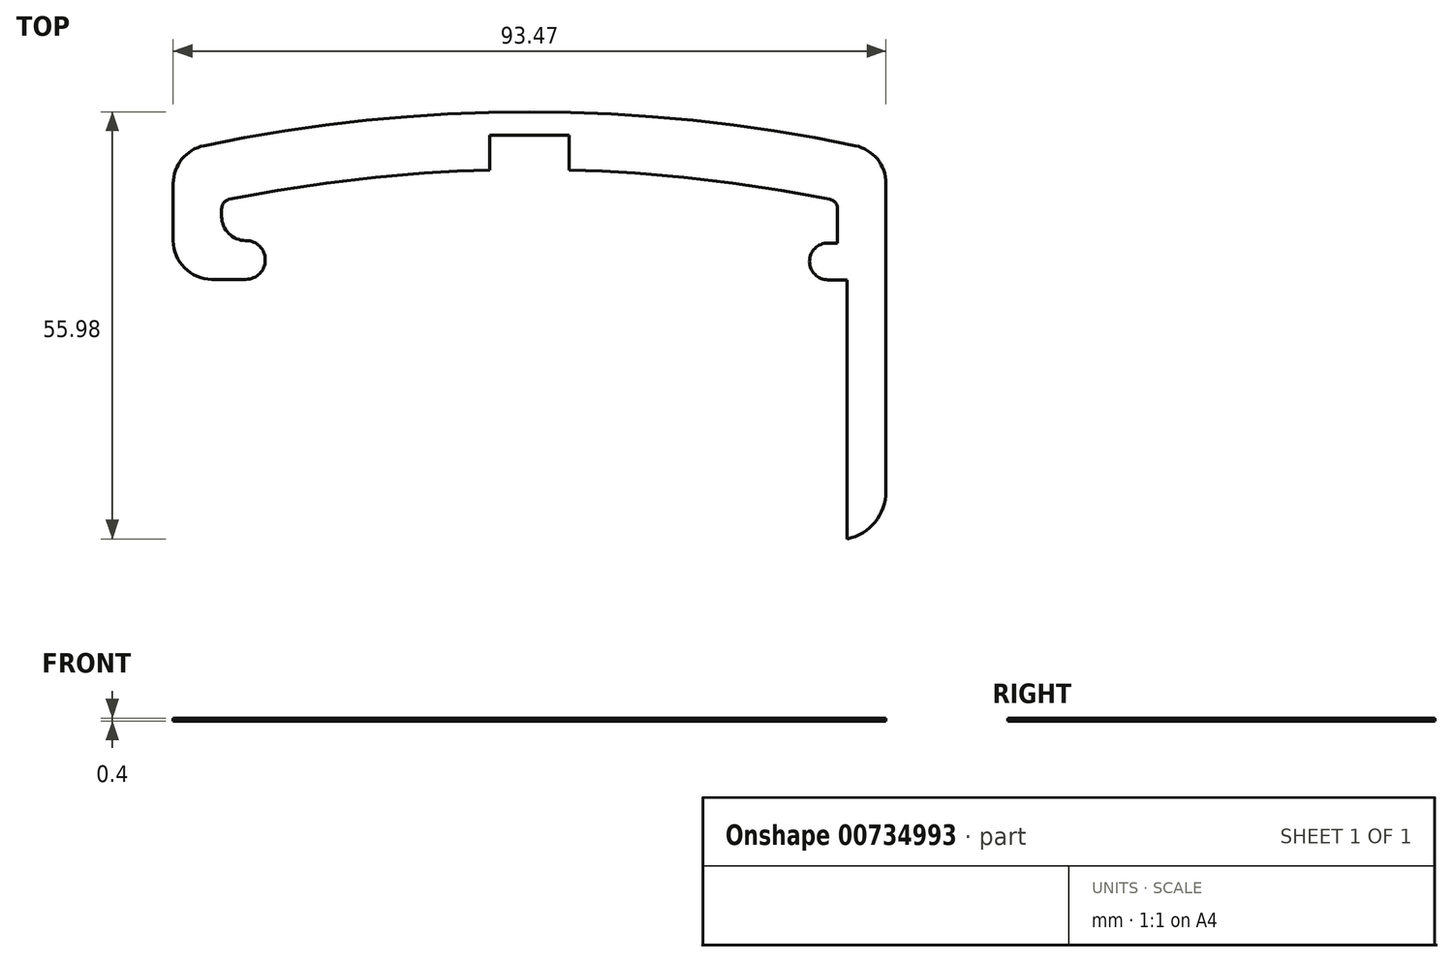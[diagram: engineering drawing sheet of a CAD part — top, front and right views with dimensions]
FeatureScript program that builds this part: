
annotation { "Feature Type Name" : "Feature", "Feature Type Description" : "" }
export const myFeature = defineFeature(function(context is Context, id is Id, definition is map)
    precondition{}
    {
        {
            assignVariable(context, id + "F0", {"name" : "THICKNESS", "anyValue" : .4});
        }
        {
            var Q0;
            Q0=qCreatedBy(makeId("Top.planeOp"),FACE);
            var sketch = newSketch(context, id + "F1", { "sketchPlane" : qUnion([Q0])});
            skLineSegment(sketch, "E0", {"start": v(0, -38.1) * mm, "end": v(0, 0) * mm});
            skLineSegment(sketch, "E1", {"start": v(-40.39, -196.85) * mm, "end": v(-40.39, 86.17) * mm, "construction": true});
            skArc(sketch, "E2", {"start": v(0, 0) * mm, "mid": v(-20.09, 3.07) * mm, "end": v(-40.39, 4.1) * mm});
            skArc(sketch, "E3.MirrorCS", {"start": v(-80.77, 0) * mm, "mid": v(-60.68, 3.07) * mm, "end": v(-40.39, 4.1) * mm});
            skLineSegment(sketch, "E4", {"start": v(0, -38.1) * mm, "end": v(6.35, -38.1) * mm});
            skLineSegment(sketch, "E5", {"start": v(6.35, -38.1) * mm, "end": v(6.35, 6.35) * mm});
            skLineSegment(sketch, "E6", {"start": v(-80.77, 0) * mm, "end": v(-80.77, -2.03) * mm});
            skArc(sketch, "E7", {"start": v(-80.77, -2.03) * mm, "mid": v(-79.84, -4.28) * mm, "end": v(-77.6, -5.2) * mm});
            skArc(sketch, "E8", {"start": v(-77.6, -5.2) * mm, "mid": v(-75.06, -7.75) * mm, "end": v(-77.6, -10.29) * mm});
            skArc(sketch, "E9", {"start": v(6.35, 6.35) * mm, "mid": v(-16.87, 10.32) * mm, "end": v(-40.39, 11.66) * mm});
            skArc(sketch, "E10.MirrorCS", {"start": v(-87.12, 6.35) * mm, "mid": v(-63.9, 10.32) * mm, "end": v(-40.39, 11.66) * mm});
            skLineSegment(sketch, "E11", {"start": v(-87.12, 6.35) * mm, "end": v(-87.12, -10.29) * mm});
            skArc(sketch, "E12", {"start": v(6.35, -38.1) * mm, "mid": v(4.5, -42.6) * mm, "end": v(0, -44.45) * mm});
            skLineSegment(sketch, "E13", {"start": v(0, -38.1) * mm, "end": v(0, -44.45) * mm});
            skLineSegment(sketch, "E14", {"start": v(-77.6, -10.29) * mm, "end": v(-87.12, -10.29) * mm});
            skSolve(sketch);
        }
        {
            var Q0;
            Q0=qSketchRegion(id+"F1",true);
            extrude(context, id + "F2", {"entities" : qUnion([Q0]), "depth" : (getVariable(context, 'THICKNESS')) * mm, "offsetDistance" : 25.4 * mm});
        }
        {
            var Q0;
            Q0=qCreatedBy(makeId("Top.planeOp"),FACE);
            var sketch = newSketch(context, id + "F3", { "sketchPlane" : qUnion([Q0])});
            skLineSegment(sketch, "E15.bottom", {"start": v(0, -5.52) * mm, "end": v(-1.27, -5.52) * mm});
            skLineSegment(sketch, "E15.top", {"start": v(0, -10.35) * mm, "end": v(-1.27, -10.35) * mm});
            skLineSegment(sketch, "E15.left", {"start": v(0, -5.52) * mm, "end": v(0, -10.35) * mm});
            skLineSegment(sketch, "E15.right", {"start": v(-1.27, -5.52) * mm, "end": v(-1.27, -10.35) * mm});
            skArc(sketch, "E16", {"start": v(-1.27, -5.52) * mm, "mid": v(-3.68, -7.94) * mm, "end": v(-1.27, -10.35) * mm});
            skSolve(sketch);
        }
        {
            var Q0;
            Q0=qSketchRegion(id+"F3",true);
            extrude(context, id + "F4", {"entities" : qUnion([Q0]), "operationType" : NewBodyOperationType.ADD, "depth" : (getVariable(context, 'THICKNESS')) * mm, "offsetDistance" : 25.4 * mm});
        }
        {
            var Q0;
            Q0=makeQuery(id+"F4.boolean.opBoolean","MERGE",FACE,{"derivedFrom":[makeQuery(id+"F2.opExtrude","CAP_FACE",FACE,{"disambiguationData":[OSD([sQuery(id+"F1.wireOp",EDGE,"E0"),sQuery(id+"F1.wireOp",EDGE,"E2"),sQuery(id+"F1.wireOp",EDGE,"E3.MirrorCS"),sQuery(id+"F1.wireOp",EDGE,"E5"),sQuery(id+"F1.wireOp",EDGE,"E6"),sQuery(id+"F1.wireOp",EDGE,"E7"),sQuery(id+"F1.wireOp",EDGE,"E8"),sQuery(id+"F1.wireOp",EDGE,"E9"),sQuery(id+"F1.wireOp",EDGE,"E10.MirrorCS"),sQuery(id+"F1.wireOp",EDGE,"E11"),sQuery(id+"F1.wireOp",EDGE,"E12"),sQuery(id+"F1.wireOp",EDGE,"E13"),sQuery(id+"F1.wireOp",EDGE,"E14")])],"isStart":false}),makeQuery(id+"F4.opExtrude","CAP_FACE",FACE,{"disambiguationData":[OSD([sQuery(id+"F3.wireOp",EDGE,"2xCA8WZk-R5Xw-jf9k-nI4M-tNFU53K7TKDJ")])],"isStart":false})]});
            var sketch = newSketch(context, id + "F5", { "sketchPlane" : qUnion([Q0])});
            skLineSegment(sketch, "E17.bottom", {"start": v(0, -10.35) * mm, "end": v(1.27, -10.35) * mm});
            skLineSegment(sketch, "E17.top", {"start": v(0, -61.15) * mm, "end": v(1.27, -61.15) * mm});
            skLineSegment(sketch, "E17.left", {"start": v(0, -10.35) * mm, "end": v(0, -61.15) * mm});
            skLineSegment(sketch, "E17.right", {"start": v(1.27, -10.35) * mm, "end": v(1.27, -61.15) * mm});
            skSolve(sketch);
        }
        {
            var Q0;
            Q0 = qSketchRegion(id + "F5", true);
            extrude(context, id + "F6", {"entities" : qUnion([Q0]), "operationType" : NewBodyOperationType.REMOVE, "oppositeDirection" : true, "depth" : (getVariable(context, 'THICKNESS')) * mm, "offsetDistance" : 25.4 * mm});
        }
        {
            var Q0;
            Q0=makeQuery(id+"F2.opExtrude","SWEPT_EDGE",EDGE,{"disambiguationData":[OSD([sQuery(id+"F1.wireOp",EDGE,"E10.MirrorCS"),sQuery(id+"F1.wireOp",EDGE,"E11")])]});
            var Q1;
            Q1=makeQuery(id+"F2.opExtrude","SWEPT_EDGE",EDGE,{"disambiguationData":[OSD([sQuery(id+"F1.wireOp",EDGE,"E5"),sQuery(id+"F1.wireOp",EDGE,"E9")])]});
            var Q2;
            Q2=makeQuery(id+"F2.opExtrude","SWEPT_EDGE",EDGE,{"disambiguationData":[OSD([sQuery(id+"F1.wireOp",EDGE,"E11"),sQuery(id+"F1.wireOp",EDGE,"nPjlojTF-CVGx-MTEt-pRxP-OlM7tPyFeRFX")])]});
            fillet(context, id + "F7", {"entities" : qUnion([Q0, Q1, Q2]), "radius" : 5.08 * mm, "tangentPropagation" : true, "allowEdgeOverflow" : false});
        }
        {
            var Q0;
            Q0=makeQuery(id+"F2.opExtrude","SWEPT_EDGE",EDGE,{"disambiguationData":[OSD([sQuery(id+"F1.wireOp",EDGE,"E0"),sQuery(id+"F1.wireOp",EDGE,"E2")])]});
            var Q1;
            Q1=makeQuery(id+"F2.opExtrude","SWEPT_EDGE",EDGE,{"disambiguationData":[OSD([sQuery(id+"F1.wireOp",EDGE,"E3.MirrorCS"),sQuery(id+"F1.wireOp",EDGE,"E6")])]});
            fillet(context, id + "F8", {"entities" : qUnion([Q0, Q1]), "radius" : 1.27 * mm, "tangentPropagation" : true, "allowEdgeOverflow" : false});
        }
        {
            var Q0;
            Q0=makeQuery(id+"F4.boolean.opBoolean","MERGE",FACE,{"derivedFrom":[makeQuery(id+"F2.opExtrude","CAP_FACE",FACE,{"disambiguationData":[OSD([sQuery(id+"F1.wireOp",EDGE,"E0"),sQuery(id+"F1.wireOp",EDGE,"E2"),sQuery(id+"F1.wireOp",EDGE,"E3.MirrorCS"),sQuery(id+"F1.wireOp",EDGE,"E5"),sQuery(id+"F1.wireOp",EDGE,"E6"),sQuery(id+"F1.wireOp",EDGE,"E7"),sQuery(id+"F1.wireOp",EDGE,"E8"),sQuery(id+"F1.wireOp",EDGE,"E9"),sQuery(id+"F1.wireOp",EDGE,"E10.MirrorCS"),sQuery(id+"F1.wireOp",EDGE,"E11"),sQuery(id+"F1.wireOp",EDGE,"E12"),sQuery(id+"F1.wireOp",EDGE,"E13"),sQuery(id+"F1.wireOp",EDGE,"E14")])],"isStart":false}),makeQuery(id+"F4.opExtrude","CAP_FACE",FACE,{"disambiguationData":[OSD([sQuery(id+"F3.wireOp",EDGE,"2xCA8WZk-R5Xw-jf9k-nI4M-tNFU53K7TKDJ")])],"isStart":false})]});
            var sketch = newSketch(context, id + "F9", { "sketchPlane" : qUnion([Q0])});
            skLineSegment(sketch, "E18.bottom", {"start": v(-40.39, 3.56) * mm, "end": v(-35.18, 3.56) * mm});
            skLineSegment(sketch, "E18.top", {"start": v(-40.39, 8.64) * mm, "end": v(-35.18, 8.64) * mm});
            skLineSegment(sketch, "E18.left", {"start": v(-40.39, 3.56) * mm, "end": v(-40.39, 8.64) * mm});
            skLineSegment(sketch, "E18.right", {"start": v(-35.18, 3.56) * mm, "end": v(-35.18, 8.64) * mm});
            skLineSegment(sketch, "E19.MirrorCS", {"start": v(-40.39, 8.64) * mm, "end": v(-45.6, 8.64) * mm});
            skLineSegment(sketch, "E20.MirrorCS", {"start": v(-45.6, 3.56) * mm, "end": v(-45.6, 8.64) * mm});
            skLineSegment(sketch, "E21.MirrorCS", {"start": v(-40.39, 3.56) * mm, "end": v(-45.6, 3.56) * mm});
            skSolve(sketch);
        }
        {
            var Q0;
            Q0 = qSketchRegion(id + "F9", true);
            extrude(context, id + "F10", {"entities" : qUnion([Q0]), "operationType" : NewBodyOperationType.REMOVE, "oppositeDirection" : true, "depth" : (getVariable(context, 'THICKNESS')) * mm, "offsetDistance" : 25.4 * mm});
        }
    });
